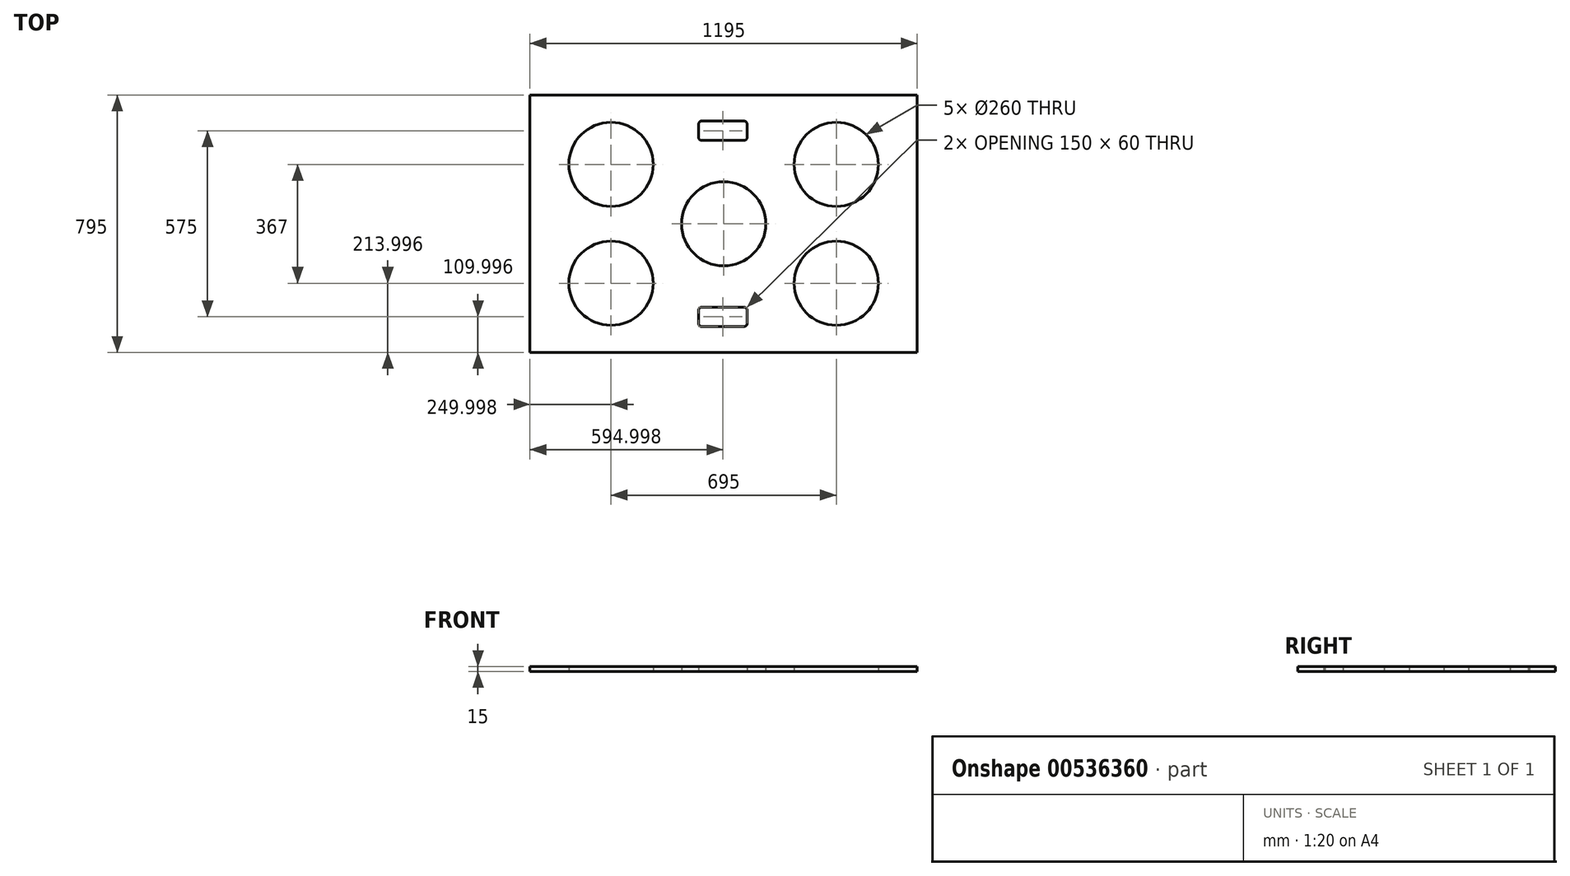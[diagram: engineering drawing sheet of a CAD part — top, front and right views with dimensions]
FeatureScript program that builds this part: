
annotation { "Feature Type Name" : "Feature", "Feature Type Description" : "" }
export const myFeature = defineFeature(function(context is Context, id is Id, definition is map)
    precondition{}
    {
        {
            var Q0;
            Q0=qCreatedBy(makeId("Top.planeOp"),FACE);
            var sketch = newSketch(context, id + "F0", { "sketchPlane" : qUnion([Q0])});
            skCircle(sketch, "E0", {"center": v(97.48, 294.59) * mm, "radius": 130 * mm});
            skCircle(sketch, "E1", {"center": v(792.48, -72.41) * mm, "radius": 130 * mm});
            skCircle(sketch, "E2", {"center": v(97.48, -72.41) * mm, "radius": 130 * mm});
            skCircle(sketch, "E3", {"center": v(792.48, 294.59) * mm, "radius": 130 * mm});
            skCircle(sketch, "E4", {"center": v(444.98, 111.09) * mm, "radius": 130 * mm});
            skPoint(sketch, "E5.visualSharp", {"position": v(1042.48, 508.59) * mm});
            skPoint(sketch, "E6.visualSharp", {"position": v(1042.48, -286.41) * mm});
            skPoint(sketch, "E7.visualSharp", {"position": v(-152.52, -286.41) * mm});
            skLineSegment(sketch, "E8.bottom", {"start": v(1042.48, 508.59) * mm, "end": v(-152.52, 508.59) * mm});
            skLineSegment(sketch, "E8.top", {"start": v(1042.48, -286.41) * mm, "end": v(-152.52, -286.41) * mm});
            skLineSegment(sketch, "E8.left", {"start": v(1042.48, 508.59) * mm, "end": v(1042.48, -286.41) * mm});
            skLineSegment(sketch, "E8.right", {"start": v(-152.52, 508.59) * mm, "end": v(-152.52, -286.41) * mm});
            skLineSegment(sketch, "E9.bottom", {"start": v(377.48, 428.59) * mm, "end": v(507.48, 428.59) * mm});
            skLineSegment(sketch, "E9.top", {"start": v(377.48, 368.59) * mm, "end": v(507.48, 368.59) * mm});
            skLineSegment(sketch, "E9.left", {"start": v(367.48, 418.59) * mm, "end": v(367.48, 378.59) * mm});
            skLineSegment(sketch, "E9.right", {"start": v(517.48, 418.59) * mm, "end": v(517.48, 378.59) * mm});
            skLineSegment(sketch, "E10.bottom", {"start": v(377.48, -146.41) * mm, "end": v(507.48, -146.41) * mm});
            skLineSegment(sketch, "E10.top", {"start": v(377.48, -206.41) * mm, "end": v(507.48, -206.41) * mm});
            skLineSegment(sketch, "E10.left", {"start": v(367.48, -156.41) * mm, "end": v(367.48, -196.41) * mm});
            skLineSegment(sketch, "E10.right", {"start": v(517.48, -156.41) * mm, "end": v(517.48, -196.41) * mm});
            skPoint(sketch, "E11.visualSharp", {"position": v(367.48, 428.59) * mm});
            skArc(sketch, "E11.filletArc", {"start": v(377.48, 428.59) * mm, "mid": v(370.4, 425.66) * mm, "end": v(367.48, 418.59) * mm});
            skPoint(sketch, "E12.visualSharp", {"position": v(367.48, 368.59) * mm});
            skArc(sketch, "E12.filletArc", {"start": v(367.48, 378.59) * mm, "mid": v(370.4, 371.52) * mm, "end": v(377.48, 368.59) * mm});
            skPoint(sketch, "E13.visualSharp", {"position": v(517.48, 368.59) * mm});
            skArc(sketch, "E13.filletArc", {"start": v(507.48, 368.59) * mm, "mid": v(514.55, 371.52) * mm, "end": v(517.48, 378.59) * mm});
            skPoint(sketch, "E14.visualSharp", {"position": v(517.48, 428.59) * mm});
            skArc(sketch, "E14.filletArc", {"start": v(517.48, 418.59) * mm, "mid": v(514.55, 425.66) * mm, "end": v(507.48, 428.59) * mm});
            skPoint(sketch, "E15.visualSharp", {"position": v(517.48, -146.41) * mm});
            skArc(sketch, "E15.filletArc", {"start": v(517.48, -156.41) * mm, "mid": v(514.55, -149.34) * mm, "end": v(507.48, -146.41) * mm});
            skPoint(sketch, "E16.visualSharp", {"position": v(517.48, -206.41) * mm});
            skArc(sketch, "E16.filletArc", {"start": v(507.48, -206.41) * mm, "mid": v(514.55, -203.48) * mm, "end": v(517.48, -196.41) * mm});
            skPoint(sketch, "E17.visualSharp", {"position": v(367.48, -206.41) * mm});
            skArc(sketch, "E17.filletArc", {"start": v(367.48, -196.41) * mm, "mid": v(370.4, -203.48) * mm, "end": v(377.48, -206.41) * mm});
            skPoint(sketch, "E18.visualSharp", {"position": v(367.48, -146.41) * mm});
            skArc(sketch, "E18.filletArc", {"start": v(377.48, -146.41) * mm, "mid": v(370.4, -149.34) * mm, "end": v(367.48, -156.41) * mm});
            skSolve(sketch);
        }
        {
            var Q0;
            Q0=makeQuery(id+"F0.imprint","IMPRINT",FACE,{"disambiguationData":[TD([[makeQuery(id+"F0.imprint","IMPRINT",EDGE,{"derivedFrom":sQuery(id+"F0.wireOp",EDGE,"E0")}),-1.0]])]});
            extrude(context, id + "F1", {"entities" : qUnion([Q0]), "depth" : 15 * mm, "offsetDistance" : 25 * mm});
        }
    });
